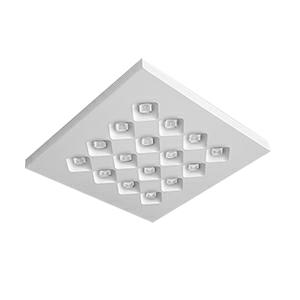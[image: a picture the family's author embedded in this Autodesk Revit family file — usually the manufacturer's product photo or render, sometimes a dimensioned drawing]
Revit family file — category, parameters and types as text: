
# Revit family: 3f_filippi_-_3f_diagon_3f_filippi_-_23031_a0686_-_3f_diagon_39w-840_dali_596x596___corn_plaf__87d4
name_source: partatom
category: Lighting Fixtures
units: mm (PartAtom-declared; Revit-internal decimal feet)

## family parameters
Cut with Voids When Loaded = No
Host = Face
Light Source = No
Part Type = Normal
Room Calculation Point = No
Round Connector Dimension = Use Diameter
Shared = No

## types (1)
- 3F Filippi - 3F Dìagon (1 x LED, 5796 lm, 40 W, 4000 K)
    Apparent Load = 40 VA
    Approval mark = CE
    CIE Flux Codes = 67 96 100 100 100
    Color Rendering = 80
    Color Temperature = 4000 K
    Control Gear = Electronic transformer
    Default Elevation = 1800 mm
    Description = ILLUMINOTECHNICAL
Luminous efficiency 100% (DLOR 100%, ULOR 0%).
Initial luminous flux of the luminaire 5796 lm.
Direct symmetric distribution.
Installation Interdistance Transv.D = 1.39 x hu - Long.D = 1.39 x hu.
Average luminance <3000 cd/m² for radial angles >65°.
Tabular UGR (CIE 117 - 4H-8H; S=0.25H; 70/50/20): RUG 18.4 - 18.4.
Beam angle: 93° - 92°.
Luminous efficacy 145 lm/W.
Lifetime (L90/B10): 30000 h. (tq+25°C)
Lifetime (L85/B10): 50000 h. (tq+25°C)
Lifetime (L80/B20): 80000 h. (tq+25°C)
Lifetime (L70/B20): 100000 h. (tq+25°C)
Sudden decreased luminous flux after 50000 hours: 0% (C0).
Photobiological safety in compliance with IEC/TR 62778: RG0 risk exempt, (IEC 62471).
In compliance with IEC/EN 62722-2-1 - IEC/EN 62717 standards.

SOURCE
Squared LED module 39W/840.
Energy efficiency class (UE 2019/2020 - UE 2019/2015): C.
CIE 13.3 Colour rendering index: CRI >80 (R9 <50%).
IES TM-30 Fidelity Index: Rf = 84 Rg = 95.
CCT nominal colour temperature 4000 K.
Colour initial tolerance (MacAdam): SDCM 3.

MECHANICAL
Housing in hot-galvanised steel, painted in white polyester.
Honeycombed diagonal screen in white anti-glare polycarbonate.
Rhomboidal lenses with differentiated surfaces, etched and prismatic to optimise the orientation of the luminous flux, in transparent methacrylate (PMMA).
Luminaire with limited surface temperature. - D - (EN 60598-2-24)
Dimensions: 600x600 mm, height 40 mm. Weight 6.195 kg.
IP43 protection degree for exposed part, IP20 for recessed part.
Mechanical strength to impacts IK06 (1 joule).
Glow-wire test resistance 650°C.

ELECTRICAL
Halogen Free DALI-2 DATI (Parts 251, 252, 253), PUSH-DIM, electronic wiring 230V-50/60Hz, power factor 0.97 at full load, THD <25%, constant output current, class I, 1 driver, 1 DALI addresse.
Power of the luminaire 40 W.
ENEC - CE.
SAFE FLICKER: PstLM=<1 and SVM=<0.4 (IEC TR 61547-1 and IEC TR 63158), to ensure a more comfortable and safe light.
Luminaire compliant with EN 60598-2-22 for power supply from a centralised emergency system CPSS (Central Power Supply System), not incorporated in the luminaire - high risk areas excluded. The default power and flux are 100% in AC and 15% in DC.
Ambient temperature from 0°C to +25°C.
Temperature class T6 max 85°C.
Quick connection.
Relative humidity UR: <85%.

INSTALLATION
Ceiling.
Height only 40 mm.
All accessories dedicated to this product are available on the Catalog and on our website www.3F-Filippi.com.

ACCESSORIES
A0686 - 596x596 Diagon frame for Ceiling installation.

APPLICATIONS
Environments: staterooms, with VDTs, offices.
Environments with exacting visual tasks, where diffused soft light for optimum visual comfort is required.

LIGHT MANAGEMENT
Recommended minimum setting: 10%.
The luminaire, equipped with (DALI-2 DATI) driver, can be controlled manually with 3F Easy Dim technology or automatically/manually with wired or wireless DALI/D2D control systems.
The D2D driver guarantees interoperability with other devices with the same certification by making the following information available:
Device Data (Part 251), Energy Report (Part 252), Diagnosis & Maintenance (Part 253).
In electrical systems without a regulation system (manual or automatic) and DALI bus, a suitable jumper must be made on the DA-DA terminals of the appliance.

WARNING
Luminaire designed for disposal/recycling at end-of-life.
Replaceable (LED only) light source by a professional. Replaceable control gear by a professional.
    Height = 0 mm  [stored 0 ft]
    Lamp = 1 x LED
    Lamp Light Flux = 5796 lm
    Lamp Power = 40 W
    Lamp count = 1
    Length = 600 mm
    Lifetime = 50000 h
    Luminous efficacy = 145 lm/W
    Manufacturer = 3F Filippi
    ModVariant = No
    Model = 3F Filippi - 23031+A0686 - 3F Diagon 39W-840 DALI 596x596 + Corn.plaf.
    Mounting Place = Ceiling
    Mounting Type = Recessed
    Number of Poles = 1
    OnlyDefault = Yes
    Power Factor = 1
    Product Name = 3F Filippi - 3F Dìagon
    Product group = recessed luminaire
    ProductGroupID = 4
    Protection Class = Protection class I
    Protection Degree = IP 20
    RLX_Detail_Level = 1
    RLX_Emergency_Light_Flux = 0 lm
    RLX_Emergency_Type = 0
    RLX_Emergency_Type_DB = No
    RlxData = <blob elided: 98497 chars, md5=9d0f2065>
    Socket = socket
    Standby Power = 0 W
    System Light Flux = 5796 lm
    System Power = 40 W
    Type Comments = Product without accessories
    Type Image = 3ffilippi_3f_diagon__a0686.jpg
    URL = http://relux.com
    VarID = ---
    Voltage = 0 V
    Weight = 0.00 kg
    Width = 600 mm

note: [stored X ft] marks values corroborated as IEEE doubles in the binary element streams (Revit-internal decimal feet)

## geometry (parser evidence)
native form markers: Blend x4, Sweep x8
no freeform markers — native parametric forms only
